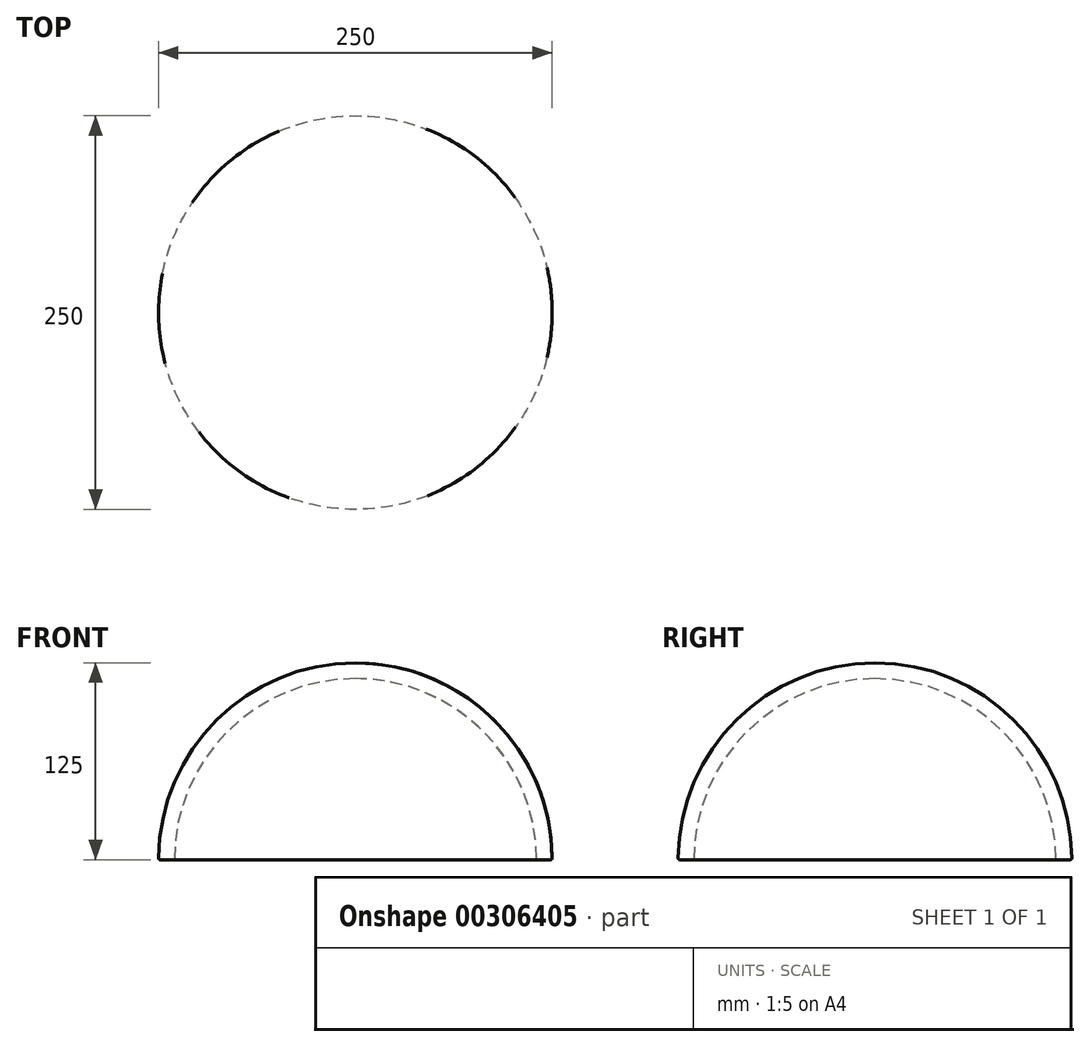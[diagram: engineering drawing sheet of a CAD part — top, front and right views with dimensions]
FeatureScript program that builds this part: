
annotation { "Feature Type Name" : "Feature", "Feature Type Description" : "" }
export const myFeature = defineFeature(function(context is Context, id is Id, definition is map)
    precondition{}
    {
        {
            var Q0;
            Q0=qCreatedBy(makeId("Front.planeOp"),FACE);
            var sketch = newSketch(context, id + "F0", { "sketchPlane" : qUnion([Q0])});
            skArc(sketch, "E0", {"start": v(-125, 0) * mm, "mid": v(0, 125) * mm, "end": v(125, 0) * mm});
            skArc(sketch, "E1.0", {"start": v(-115, 0) * mm, "mid": v(0, 115) * mm, "end": v(115, 0) * mm});
            skLineSegment(sketch, "E2", {"start": v(-125, 0) * mm, "end": v(-115, 0) * mm});
            skLineSegment(sketch, "E3", {"start": v(115, 0) * mm, "end": v(125, 0) * mm});
            skLineSegment(sketch, "E4", {"start": v(0, 0) * mm, "end": v(0, 42.6) * mm});
            skLineSegment(sketch, "E5", {"start": v(0, 128.79) * mm, "end": v(0, 0) * mm});
            skPoint(sketch, "E5.startSnap0", {"position": v(0, 125) * mm});
            skSolve(sketch);
        }
        {
            var Q0;
            {var subQ0=sQuery(id+"F0.wireOp",EDGE,"E3");Q0=makeQuery(id+"F0.imprint","IMPRINT",FACE,{"disambiguationData":[TD([[makeQuery(id+"F0.imprint","IMPRINT",EDGE,{"derivedFrom":subQ0}),1.0]])]});}
            var Q1;
            Q1=sQuery(id+"F0.wireOp",EDGE,"E5");
            revolve(context, id + "F1", {"entities" : qUnion([Q0]), "axis" : qUnion([Q1]), "revolveType" : RevolveType.FULL});
        }
        {
            var Q0;
            Q0=makeQuery(id+"F1.opRevolve","SWEPT_EDGE",EDGE,{"disambiguationData":[OSD([sQuery(id+"F0.wireOp",EDGE,"E0"),sQuery(id+"F0.wireOp",EDGE,"E3")])]});
            var Q1;
            Q1=makeQuery(id+"F1.opRevolve","SWEPT_EDGE",EDGE,{"disambiguationData":[OSD([sQuery(id+"F0.wireOp",EDGE,"E1.0"),sQuery(id+"F0.wireOp",EDGE,"E3")])]});
            fillet(context, id + "F2", {"entities" : qUnion([Q0, Q1]), "radius" : 1 * mm, "tangentPropagation" : true, "allowEdgeOverflow" : false});
        }
    });
